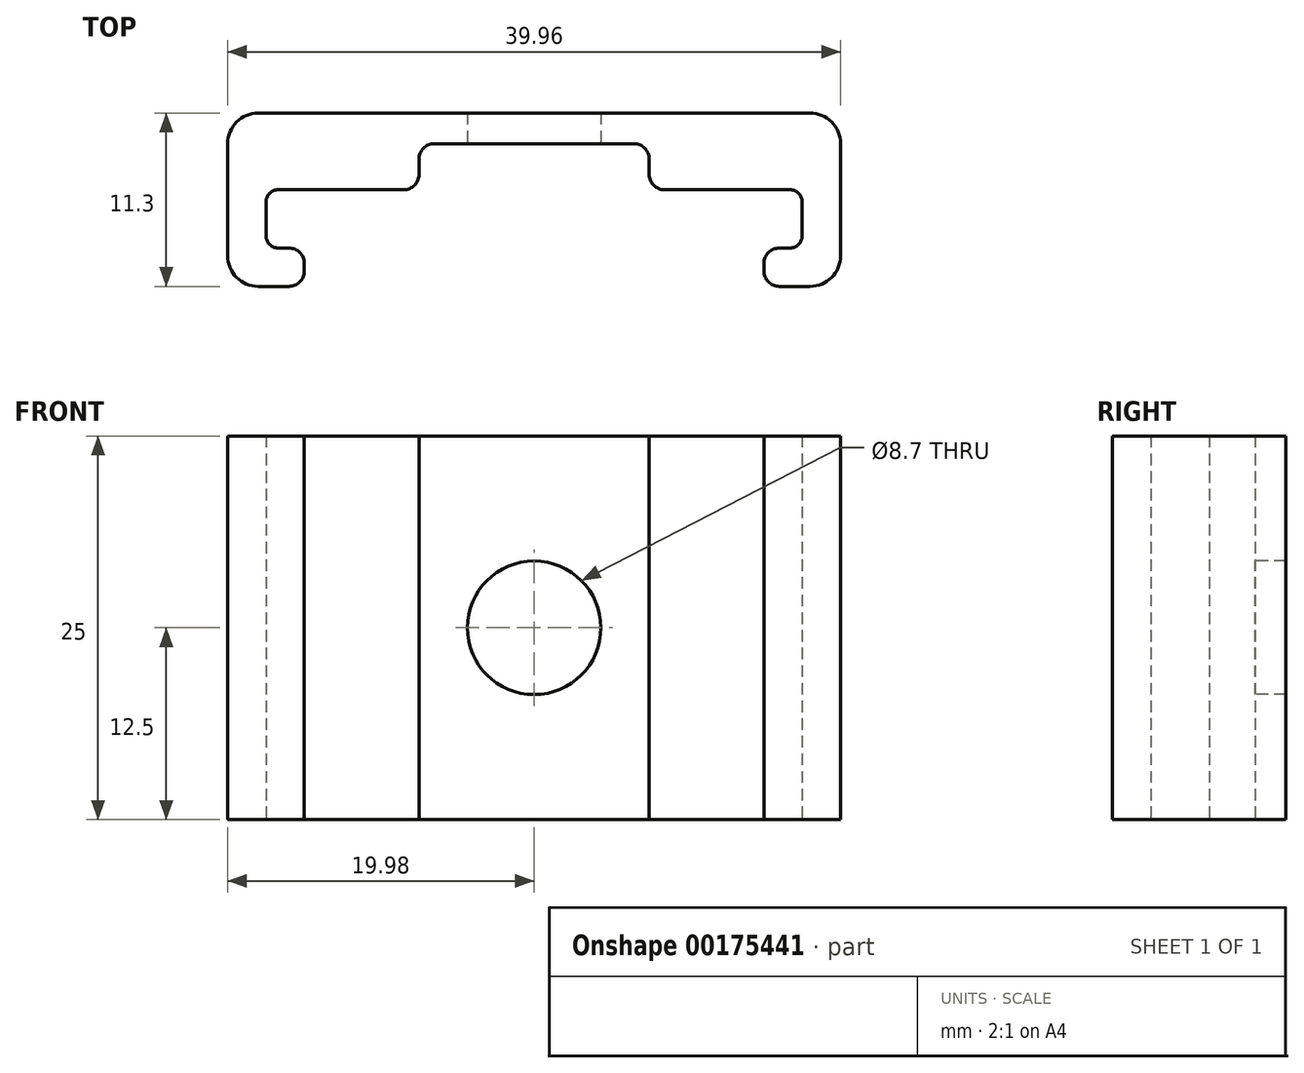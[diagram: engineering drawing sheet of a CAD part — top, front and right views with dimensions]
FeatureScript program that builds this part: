
annotation { "Feature Type Name" : "Feature", "Feature Type Description" : "" }
export const myFeature = defineFeature(function(context is Context, id is Id, definition is map)
    precondition{}
    {
        {
            var Q0;
            Q0=qCreatedBy(makeId("Top.planeOp"),FACE);
            var sketch = newSketch(context, id + "F0", { "sketchPlane" : qUnion([Q0])});
            skLineSegment(sketch, "E0", {"start": v(-14.97, -8.8) * mm, "end": v(-14.97, -11.3) * mm});
            skLineSegment(sketch, "E1", {"start": v(-14.97, -11.3) * mm, "end": v(-19.98, -11.3) * mm});
            skLineSegment(sketch, "E2", {"start": v(-19.97, -11.3) * mm, "end": v(-19.98, 0) * mm});
            skLineSegment(sketch, "E3", {"start": v(-19.98, 0) * mm, "end": v(0, 0) * mm});
            skLineSegment(sketch, "E4", {"start": v(-7.5, -5) * mm, "end": v(-17.48, -5) * mm});
            skLineSegment(sketch, "E5", {"start": v(-17.48, -5) * mm, "end": v(-17.48, -8.8) * mm});
            skLineSegment(sketch, "E6", {"start": v(-17.48, -8.8) * mm, "end": v(-14.97, -8.8) * mm});
            skLineSegment(sketch, "E7.MirrorCS", {"start": v(17.48, -5) * mm, "end": v(17.48, -8.8) * mm});
            skLineSegment(sketch, "E8.MirrorCS", {"start": v(19.98, 0) * mm, "end": v(0, 0) * mm});
            skLineSegment(sketch, "E9.MirrorCS", {"start": v(14.97, -8.8) * mm, "end": v(14.97, -11.3) * mm});
            skLineSegment(sketch, "E10.MirrorCS", {"start": v(17.48, -8.8) * mm, "end": v(14.97, -8.8) * mm});
            skLineSegment(sketch, "E11.MirrorCS", {"start": v(19.98, -11.3) * mm, "end": v(19.98, 0) * mm});
            skLineSegment(sketch, "E12.MirrorCS", {"start": v(14.97, -11.3) * mm, "end": v(19.98, -11.3) * mm});
            skLineSegment(sketch, "E13", {"start": v(-7.5, -5) * mm, "end": v(-7.5, -2) * mm});
            skLineSegment(sketch, "E14", {"start": v(-7.5, -2) * mm, "end": v(0, -2) * mm});
            skLineSegment(sketch, "E15.MirrorCS", {"start": v(7.5, -5) * mm, "end": v(7.5, -2) * mm});
            skLineSegment(sketch, "E16.MirrorCS", {"start": v(7.5, -5) * mm, "end": v(17.48, -5) * mm});
            skLineSegment(sketch, "E17.MirrorCS", {"start": v(7.5, -2) * mm, "end": v(0, -2) * mm});
            skSolve(sketch);
        }
        {
            var Q0;
            Q0=makeQuery(id+"F0.imprint","IMPRINT",FACE,{"disambiguationData":[TD([[makeQuery(id+"F0.imprint","IMPRINT",EDGE,{"derivedFrom":sQuery(id+"F0.wireOp",EDGE,"E0")}),-1.0]])]});
            extrude(context, id + "F1", {"entities" : qUnion([Q0]), "depth" : 25 * mm});
        }
        {
            var Q0;
            Q0=makeQuery(id+"F1.opExtrude","SWEPT_EDGE",EDGE,{"disambiguationData":[OSD([sQuery(id+"F0.wireOp",EDGE,"E2"),sQuery(id+"F0.wireOp",EDGE,"E3")])]});
            var Q1;
            Q1=makeQuery(id+"F1.opExtrude","SWEPT_EDGE",EDGE,{"disambiguationData":[OSD([sQuery(id+"F0.wireOp",EDGE,"E8.MirrorCS"),sQuery(id+"F0.wireOp",EDGE,"E11.MirrorCS")])]});
            var Q2;
            Q2=makeQuery(id+"F1.opExtrude","SWEPT_EDGE",EDGE,{"disambiguationData":[OSD([sQuery(id+"F0.wireOp",EDGE,"E1"),sQuery(id+"F0.wireOp",EDGE,"E2")])]});
            var Q3;
            Q3=makeQuery(id+"F1.opExtrude","SWEPT_EDGE",EDGE,{"disambiguationData":[OSD([sQuery(id+"F0.wireOp",EDGE,"E11.MirrorCS"),sQuery(id+"F0.wireOp",EDGE,"E12.MirrorCS")])]});
            fillet(context, id + "F2", {"entities" : qUnion([Q0, Q1, Q2, Q3]), "radius" : 2 * mm, "tangentPropagation" : true, "allowEdgeOverflow" : false});
        }
        {
            var Q0;
            Q0=makeQuery(id+"F1.opExtrude","SWEPT_EDGE",EDGE,{"disambiguationData":[OSD([sQuery(id+"F0.wireOp",EDGE,"E15.MirrorCS"),sQuery(id+"F0.wireOp",EDGE,"E17.MirrorCS")])]});
            var Q1;
            Q1=makeQuery(id+"F1.opExtrude","SWEPT_EDGE",EDGE,{"disambiguationData":[OSD([sQuery(id+"F0.wireOp",EDGE,"E13"),sQuery(id+"F0.wireOp",EDGE,"E14")])]});
            var Q2;
            Q2=makeQuery(id+"F1.opExtrude","SWEPT_EDGE",EDGE,{"disambiguationData":[OSD([sQuery(id+"F0.wireOp",EDGE,"E15.MirrorCS"),sQuery(id+"F0.wireOp",EDGE,"E16.MirrorCS")])]});
            var Q3;
            Q3=makeQuery(id+"F1.opExtrude","SWEPT_EDGE",EDGE,{"disambiguationData":[OSD([sQuery(id+"F0.wireOp",EDGE,"E4"),sQuery(id+"F0.wireOp",EDGE,"E13")])]});
            var Q4;
            Q4=makeQuery(id+"F1.opExtrude","SWEPT_EDGE",EDGE,{"disambiguationData":[OSD([sQuery(id+"F0.wireOp",EDGE,"E0"),sQuery(id+"F0.wireOp",EDGE,"E1")])]});
            var Q5;
            Q5=makeQuery(id+"F1.opExtrude","SWEPT_EDGE",EDGE,{"disambiguationData":[OSD([sQuery(id+"F0.wireOp",EDGE,"E0"),sQuery(id+"F0.wireOp",EDGE,"E6")])]});
            var Q6;
            Q6=makeQuery(id+"F1.opExtrude","SWEPT_EDGE",EDGE,{"disambiguationData":[OSD([sQuery(id+"F0.wireOp",EDGE,"E9.MirrorCS"),sQuery(id+"F0.wireOp",EDGE,"E10.MirrorCS")])]});
            var Q7;
            Q7=makeQuery(id+"F1.opExtrude","SWEPT_EDGE",EDGE,{"disambiguationData":[OSD([sQuery(id+"F0.wireOp",EDGE,"E9.MirrorCS"),sQuery(id+"F0.wireOp",EDGE,"E12.MirrorCS")])]});
            fillet(context, id + "F3", {"entities" : qUnion([Q0, Q1, Q2, Q3, Q4, Q5, Q6, Q7]), "radius" : 1 * mm, "tangentPropagation" : true, "allowEdgeOverflow" : false});
        }
        {
            var Q0;
            Q0=makeQuery(id+"F1.opExtrude","SWEPT_EDGE",EDGE,{"disambiguationData":[OSD([sQuery(id+"F0.wireOp",EDGE,"E7.MirrorCS"),sQuery(id+"F0.wireOp",EDGE,"E16.MirrorCS")])]});
            var Q1;
            Q1=makeQuery(id+"F1.opExtrude","SWEPT_EDGE",EDGE,{"disambiguationData":[OSD([sQuery(id+"F0.wireOp",EDGE,"E4"),sQuery(id+"F0.wireOp",EDGE,"E5")])]});
            var Q2;
            Q2=makeQuery(id+"F1.opExtrude","SWEPT_EDGE",EDGE,{"disambiguationData":[OSD([sQuery(id+"F0.wireOp",EDGE,"E5"),sQuery(id+"F0.wireOp",EDGE,"E6")])]});
            var Q3;
            Q3=makeQuery(id+"F1.opExtrude","SWEPT_EDGE",EDGE,{"disambiguationData":[OSD([sQuery(id+"F0.wireOp",EDGE,"E7.MirrorCS"),sQuery(id+"F0.wireOp",EDGE,"E10.MirrorCS")])]});
            fillet(context, id + "F4", {"entities" : qUnion([Q0, Q1, Q2, Q3]), "radius" : 0.8 * mm, "tangentPropagation" : true, "allowEdgeOverflow" : false});
        }
        {
            var Q0;
            Q0=makeQuery(id+"F1.opExtrude","SWEPT_FACE",FACE,{"disambiguationData":[OSD([sQuery(id+"F0.wireOp",EDGE,"E14"),sQuery(id+"F0.wireOp",EDGE,"E17.MirrorCS")])]});
            var sketch = newSketch(context, id + "F5", { "sketchPlane" : qUnion([Q0])});
            skCircle(sketch, "E18", {"center": v(0, 12.5) * mm, "radius": 4.35 * mm});
            skSolve(sketch);
        }
        {
            var Q0;
            Q0 = qSketchRegion(id + "F5", true);
            extrude(context, id + "F6", {"entities" : qUnion([Q0]), "operationType" : NewBodyOperationType.REMOVE, "oppositeDirection" : true, "depth" : 25 * mm});
        }
    });
